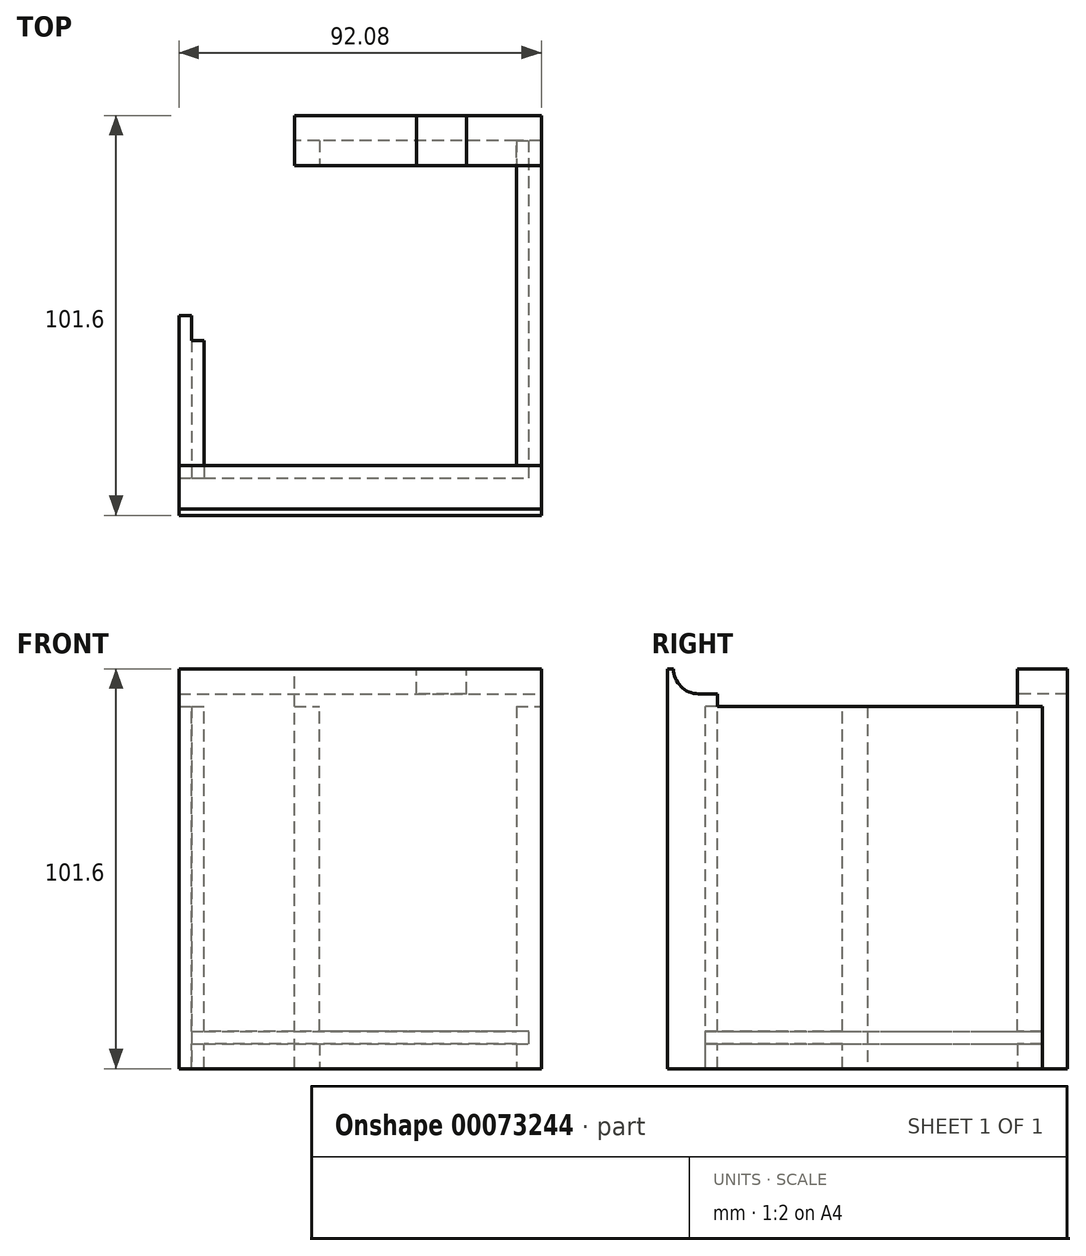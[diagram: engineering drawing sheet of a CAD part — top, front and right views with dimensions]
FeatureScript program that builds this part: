
annotation { "Feature Type Name" : "Feature", "Feature Type Description" : "" }
export const myFeature = defineFeature(function(context is Context, id is Id, definition is map)
    precondition{}
    {
        {
            var Q0;
            Q0=qCreatedBy(makeId("Top.planeOp"),FACE);
            var sketch = newSketch(context, id + "F0", { "sketchPlane" : qUnion([Q0])});
            skLineSegment(sketch, "E0", {"start": v(0, 0) * mm, "end": v(0, -101.6) * mm, "construction": true});
            skLineSegment(sketch, "E1", {"start": v(0, -101.6) * mm, "end": v(-92.08, -101.6) * mm, "construction": true});
            skLineSegment(sketch, "E2", {"start": v(-62.75, 0) * mm, "end": v(0, 0) * mm, "construction": true});
            skLineSegment(sketch, "E3", {"start": v(-92.08, -101.6) * mm, "end": v(-92.08, -50.8) * mm, "construction": true});
            skLineSegment(sketch, "E4", {"start": v(-62.75, 0) * mm, "end": v(-92.08, -50.8) * mm, "construction": true});
            skSolve(sketch);
        }
        {
            var Q0;
            Q0=qCreatedBy(makeId("Front.planeOp"),FACE);
            var sketch = newSketch(context, id + "F1", { "sketchPlane" : qUnion([Q0])});
            skLineSegment(sketch, "E5.bottom", {"start": v(0, 0) * mm, "end": v(-62.75, 0) * mm});
            skLineSegment(sketch, "E5.top", {"start": v(0, 101.6) * mm, "end": v(-62.75, 101.6) * mm});
            skLineSegment(sketch, "E5.left", {"start": v(0, 0) * mm, "end": v(0, 101.6) * mm});
            skLineSegment(sketch, "E5.right", {"start": v(-62.75, 0) * mm, "end": v(-62.75, 101.6) * mm});
            skSolve(sketch);
        }
        {
            var Q0;
            Q0=makeQuery(id+"F1.imprint","IMPRINT",FACE,{"disambiguationData":[TD([[makeQuery(id+"F1.imprint","IMPRINT",EDGE,{"derivedFrom":sQuery(id+"F1.wireOp",EDGE,"E5.bottom")}),-1.0]])]});
            extrude(context, id + "F2", {"entities" : qUnion([Q0]), "depth" : 12.7 * mm});
        }
        {
            var Q0;
            Q0=makeQuery(id+"F2.opExtrude","CAP_FACE",FACE,{"disambiguationData":[OSD([sQuery(id+"F1.wireOp",EDGE,"E5.bottom"),sQuery(id+"F1.wireOp",EDGE,"E5.top"),sQuery(id+"F1.wireOp",EDGE,"E5.left"),sQuery(id+"F1.wireOp",EDGE,"E5.right")])],"isStart":false});
            var sketch = newSketch(context, id + "F3", { "sketchPlane" : qUnion([Q0])});
            skLineSegment(sketch, "E6.bottom", {"start": v(-6.35, 92.08) * mm, "end": v(0, 92.08) * mm});
            skLineSegment(sketch, "E6.top", {"start": v(-6.35, 6.35) * mm, "end": v(0, 6.35) * mm});
            skLineSegment(sketch, "E6.left", {"start": v(-6.35, 92.08) * mm, "end": v(-6.35, 6.35) * mm});
            skLineSegment(sketch, "E6.right", {"start": v(0, 92.08) * mm, "end": v(0, 6.35) * mm});
            skLineSegment(sketch, "E7.bottom", {"start": v(-6.35, 6.35) * mm, "end": v(-62.75, 6.35) * mm});
            skLineSegment(sketch, "E7.top", {"start": v(-6.35, 9.53) * mm, "end": v(-62.75, 9.52) * mm});
            skLineSegment(sketch, "E7.left", {"start": v(-6.35, 6.35) * mm, "end": v(-6.35, 9.53) * mm});
            skLineSegment(sketch, "E7.right", {"start": v(-62.75, 6.35) * mm, "end": v(-62.75, 9.52) * mm});
            skLineSegment(sketch, "E8.bottom", {"start": v(-62.75, 9.52) * mm, "end": v(-56.4, 9.52) * mm});
            skLineSegment(sketch, "E8.top", {"start": v(-62.75, 92.08) * mm, "end": v(-56.4, 92.08) * mm});
            skLineSegment(sketch, "E8.left", {"start": v(-62.75, 9.52) * mm, "end": v(-62.75, 92.08) * mm});
            skLineSegment(sketch, "E8.right", {"start": v(-56.4, 9.52) * mm, "end": v(-56.4, 92.08) * mm});
            skLineSegment(sketch, "E9.bottom", {"start": v(-56.4, 9.52) * mm, "end": v(-62.75, 9.52) * mm});
            skLineSegment(sketch, "E9.top", {"start": v(-56.4, 0) * mm, "end": v(-62.75, 0) * mm});
            skLineSegment(sketch, "E9.left", {"start": v(-56.4, 9.52) * mm, "end": v(-56.4, 0) * mm});
            skLineSegment(sketch, "E9.right", {"start": v(-62.75, 9.52) * mm, "end": v(-62.75, 0) * mm});
            skLineSegment(sketch, "E10.bottom", {"start": v(-6.35, 9.53) * mm, "end": v(0, 9.53) * mm});
            skLineSegment(sketch, "E10.top", {"start": v(-6.35, 0) * mm, "end": v(0, 0) * mm});
            skLineSegment(sketch, "E10.left", {"start": v(-6.35, 9.53) * mm, "end": v(-6.35, 0) * mm});
            skLineSegment(sketch, "E10.right", {"start": v(0, 9.53) * mm, "end": v(0, 0) * mm});
            skSolve(sketch);
        }
        {
            var Q0;
            Q0 = qSketchRegion(id + "F3", true);
            extrude(context, id + "F4", {"entities" : qUnion([Q0]), "operationType" : NewBodyOperationType.REMOVE, "oppositeDirection" : true, "depth" : 6.35 * mm});
        }
        {
            var Q0;
            Q0=makeQuery(id+"F4.boolean.opBoolean","COPY",FACE,{"derivedFrom":makeQuery(id+"F4.opExtrude","CAP_FACE",FACE,{"disambiguationData":[OSD([sQuery(id+"F3.wireOp",EDGE,"E6.bottom"),sQuery(id+"F3.wireOp",EDGE,"E6.left"),sQuery(id+"F3.wireOp",EDGE,"E6.right"),sQuery(id+"F3.wireOp",EDGE,"E7.bottom"),sQuery(id+"F3.wireOp",EDGE,"E7.top"),sQuery(id+"F3.wireOp",EDGE,"E8.top"),sQuery(id+"F3.wireOp",EDGE,"E8.left"),sQuery(id+"F3.wireOp",EDGE,"E8.right"),sQuery(id+"F3.wireOp",EDGE,"E9.top"),sQuery(id+"F3.wireOp",EDGE,"E9.left"),sQuery(id+"F3.wireOp",EDGE,"E9.right"),sQuery(id+"F3.wireOp",EDGE,"E10.top"),sQuery(id+"F3.wireOp",EDGE,"E10.left"),sQuery(id+"F3.wireOp",EDGE,"E10.right")])],"isStart":false})});
            var sketch = newSketch(context, id + "F5", { "sketchPlane" : qUnion([Q0])});
            skLineSegment(sketch, "E11", {"start": v(-6.35, 92.08) * mm, "end": v(0, 92.08) * mm});
            skLineSegment(sketch, "E12", {"start": v(0, 92.08) * mm, "end": v(0, 0) * mm});
            skLineSegment(sketch, "E13", {"start": v(0, 0) * mm, "end": v(-6.35, 0) * mm});
            skLineSegment(sketch, "E14", {"start": v(-6.35, 0) * mm, "end": v(-6.35, 6.35) * mm});
            skLineSegment(sketch, "E15", {"start": v(-6.35, 6.35) * mm, "end": v(-3.17, 6.35) * mm});
            skLineSegment(sketch, "E16", {"start": v(-3.17, 6.35) * mm, "end": v(-3.17, 9.53) * mm});
            skLineSegment(sketch, "E17", {"start": v(-3.17, 9.53) * mm, "end": v(-6.35, 9.53) * mm});
            skLineSegment(sketch, "E18", {"start": v(-6.35, 9.53) * mm, "end": v(-6.35, 92.08) * mm});
            skSolve(sketch);
        }
        {
            var Q0;
            Q0 = qSketchRegion(id + "F5", true);
            extrude(context, id + "F6", {"entities" : qUnion([Q0]), "depth" : 85.72 * mm});
        }
        {
            var Q0;
            Q0=makeQuery(id+"F6.opExtrude","CAP_FACE",FACE,{"disambiguationData":[OSD([sQuery(id+"F5.wireOp",EDGE,"E11"),sQuery(id+"F5.wireOp",EDGE,"E12"),sQuery(id+"F5.wireOp",EDGE,"E13"),sQuery(id+"F5.wireOp",EDGE,"E14"),sQuery(id+"F5.wireOp",EDGE,"E15"),sQuery(id+"F5.wireOp",EDGE,"E16"),sQuery(id+"F5.wireOp",EDGE,"E17"),sQuery(id+"F5.wireOp",EDGE,"E18")])],"isStart":false});
            var sketch = newSketch(context, id + "F7", { "sketchPlane" : qUnion([Q0])});
            skLineSegment(sketch, "E19.bottom", {"start": v(0, 0) * mm, "end": v(-92.08, 0) * mm});
            skLineSegment(sketch, "E19.top", {"start": v(0, 101.6) * mm, "end": v(-92.08, 101.6) * mm});
            skLineSegment(sketch, "E19.left", {"start": v(0, 0) * mm, "end": v(0, 101.6) * mm});
            skLineSegment(sketch, "E19.right", {"start": v(-92.08, 0) * mm, "end": v(-92.08, 101.6) * mm});
            skSolve(sketch);
        }
        {
            var Q0;
            Q0 = qSketchRegion(id + "F7", true);
            extrude(context, id + "F8", {"entities" : qUnion([Q0]), "depth" : 9.52 * mm});
        }
        {
            var Q0;
            Q0=makeQuery(id+"F8.opExtrude","CAP_FACE",FACE,{"disambiguationData":[OSD([sQuery(id+"F7.wireOp",EDGE,"E19.bottom"),sQuery(id+"F7.wireOp",EDGE,"E19.top"),sQuery(id+"F7.wireOp",EDGE,"E19.left"),sQuery(id+"F7.wireOp",EDGE,"E19.right")])],"isStart":true});
            var sketch = newSketch(context, id + "F9", { "sketchPlane" : qUnion([Q0])});
            skLineSegment(sketch, "E20", {"start": v(0, 101.6) * mm, "end": v(92.08, 101.6) * mm});
            skLineSegment(sketch, "E21", {"start": v(92.08, 101.6) * mm, "end": v(92.08, 0) * mm, "construction": true});
            skLineSegment(sketch, "E22", {"start": v(92.08, 0) * mm, "end": v(6.35, 0) * mm});
            skLineSegment(sketch, "E23", {"start": v(6.35, 0) * mm, "end": v(6.35, 6.35) * mm});
            skLineSegment(sketch, "E24", {"start": v(6.35, 6.35) * mm, "end": v(88.9, 6.35) * mm});
            skLineSegment(sketch, "E25", {"start": v(88.9, 6.35) * mm, "end": v(88.9, 9.53) * mm});
            skLineSegment(sketch, "E26", {"start": v(88.9, 9.53) * mm, "end": v(6.35, 9.53) * mm});
            skLineSegment(sketch, "E27", {"start": v(6.35, 9.53) * mm, "end": v(6.35, 92.08) * mm});
            skLineSegment(sketch, "E28", {"start": v(6.35, 92.08) * mm, "end": v(0, 92.08) * mm});
            skLineSegment(sketch, "E29", {"start": v(0, 92.08) * mm, "end": v(0, 101.6) * mm});
            skLineSegment(sketch, "E30", {"start": v(85.73, 0) * mm, "end": v(85.73, 92.08) * mm});
            skLineSegment(sketch, "E31", {"start": v(85.73, 92.08) * mm, "end": v(92.08, 92.08) * mm});
            skLineSegment(sketch, "E32", {"start": v(92.08, 92.08) * mm, "end": v(92.08, 101.6) * mm});
            skSolve(sketch);
        }
        {
            var Q0;
            {var subQ0=sQuery(id+"F9.wireOp",EDGE,"E23");Q0=makeQuery(id+"F9.imprint","IMPRINT",FACE,{"disambiguationData":[TD([[makeQuery(id+"F9.imprint","IMPRINT",EDGE,{"derivedFrom":subQ0}),-1.0]])]});}
            var Q1;
            {var subQ0=sQuery(id+"F9.wireOp",EDGE,"E27");Q1=makeQuery(id+"F9.imprint","IMPRINT",FACE,{"disambiguationData":[TD([[makeQuery(id+"F9.imprint","IMPRINT",EDGE,{"derivedFrom":subQ0}),-1.0]])]});}
            extrude(context, id + "F10", {"entities" : qUnion([Q0, Q1]), "operationType" : NewBodyOperationType.ADD, "depth" : 3.17 * mm});
        }
        {
            var Q0;
            Q0=makeQuery(id+"F10.boolean.opBoolean","MERGE",FACE,{"derivedFrom":[makeQuery(id+"F8.opExtrude","SWEPT_FACE",FACE,{"disambiguationData":[OSD([sQuery(id+"F7.wireOp",EDGE,"E19.left")])]}),makeQuery(id+"F10.opExtrude","SWEPT_FACE",FACE,{"disambiguationData":[OSD([sQuery(id+"F9.wireOp",EDGE,"E29")])]})]});
            var sketch = newSketch(context, id + "F11", { "sketchPlane" : qUnion([Q0])});
            skArc(sketch, "E33", {"start": v(-100.01, 101.6) * mm, "mid": v(-98.15, 97.1) * mm, "end": v(-93.66, 95.25) * mm});
            skLineSegment(sketch, "E34", {"start": v(-100.01, 101.6) * mm, "end": v(-93.66, 101.6) * mm});
            skLineSegment(sketch, "E35", {"start": v(-93.66, 101.6) * mm, "end": v(-88.9, 101.6) * mm});
            skLineSegment(sketch, "E36", {"start": v(-88.9, 101.6) * mm, "end": v(-88.9, 95.25) * mm});
            skLineSegment(sketch, "E37", {"start": v(-88.9, 95.25) * mm, "end": v(-93.66, 95.25) * mm});
            skLineSegment(sketch, "E38", {"start": v(-93.66, 95.25) * mm, "end": v(-93.66, 101.6) * mm, "construction": true});
            skSolve(sketch);
        }
        {
            var Q0;
            Q0 = qSketchRegion(id + "F11", true);
            extrude(context, id + "F12", {"entities" : qUnion([Q0]), "operationType" : NewBodyOperationType.REMOVE, "endBound" : BoundingType.UP_TO_NEXT, "oppositeDirection" : true, "depth" : 25.4 * mm});
        }
        {
            var Q0;
            {var subQ0=sQuery(id+"F1.wireOp",EDGE,"E5.right");var subQ1=sQuery(id+"F1.wireOp",EDGE,"E5.left");var subQ2=sQuery(id+"F1.wireOp",EDGE,"E5.top");Q0=makeQuery(id+"F4.boolean.opBoolean","SPLIT",FACE,{"disambiguationData":[TD([makeQuery(id+"F2.opExtrude","SWEPT_FACE",FACE,{"disambiguationData":[OSD([subQ2])]})])],"derivedFrom":makeQuery(id+"F2.opExtrude","CAP_FACE",FACE,{"disambiguationData":[OSD([sQuery(id+"F1.wireOp",EDGE,"E5.bottom"),subQ2,subQ1,subQ0])],"isStart":false})});}
            var sketch = newSketch(context, id + "F13", { "sketchPlane" : qUnion([Q0])});
            skLineSegment(sketch, "E39.bottom", {"start": v(-31.75, 101.6) * mm, "end": v(-19.05, 101.6) * mm});
            skLineSegment(sketch, "E39.top", {"start": v(-31.75, 95.25) * mm, "end": v(-19.05, 95.25) * mm});
            skLineSegment(sketch, "E39.left", {"start": v(-31.75, 101.6) * mm, "end": v(-31.75, 95.25) * mm});
            skLineSegment(sketch, "E39.right", {"start": v(-19.05, 101.6) * mm, "end": v(-19.05, 95.25) * mm});
            skSolve(sketch);
        }
        {
            var Q0;
            Q0 = qSketchRegion(id + "F13", true);
            extrude(context, id + "F14", {"entities" : qUnion([Q0]), "operationType" : NewBodyOperationType.REMOVE, "endBound" : BoundingType.UP_TO_NEXT, "oppositeDirection" : true, "depth" : 25.4 * mm});
        }
        {
            var Q0;
            Q0=qCreatedBy(makeId("Top.planeOp"),FACE);
            var sketch = newSketch(context, id + "F15", { "sketchPlane" : qUnion([Q0])});
            skLineSegment(sketch, "E40.bottom", {"start": v(-92.08, -50.8) * mm, "end": v(-85.73, -50.8) * mm});
            skLineSegment(sketch, "E40.top", {"start": v(-92.08, -92.08) * mm, "end": v(-85.73, -92.08) * mm});
            skLineSegment(sketch, "E40.left", {"start": v(-92.08, -50.8) * mm, "end": v(-92.08, -92.08) * mm});
            skLineSegment(sketch, "E40.right", {"start": v(-85.73, -50.8) * mm, "end": v(-85.73, -92.08) * mm});
            skSolve(sketch);
        }
        {
            var Q0;
            Q0 = qSketchRegion(id + "F15", true);
            var Q1;
            Q1=makeQuery(id+"F6.opExtrude","SWEPT_FACE",FACE,{"disambiguationData":[OSD([sQuery(id+"F5.wireOp",EDGE,"E11")])]});
            extrude(context, id + "F16", {"entities" : qUnion([Q0]), "endBound" : BoundingType.UP_TO_SURFACE, "endBoundEntityFace" : qUnion([Q1]), "depth" : 25.4 * mm});
        }
        {
            var Q0;
            Q0=makeQuery(id+"F16.opExtrude","SWEPT_FACE",FACE,{"disambiguationData":[OSD([sQuery(id+"F15.wireOp",EDGE,"E40.right")])]});
            var sketch = newSketch(context, id + "F17", { "sketchPlane" : qUnion([Q0])});
            skLineSegment(sketch, "E41.bottom", {"start": v(-50.8, 9.53) * mm, "end": v(-92.08, 9.53) * mm});
            skLineSegment(sketch, "E41.top", {"start": v(-50.8, 6.35) * mm, "end": v(-92.08, 6.35) * mm});
            skLineSegment(sketch, "E41.left", {"start": v(-50.8, 9.52) * mm, "end": v(-50.8, 6.35) * mm});
            skLineSegment(sketch, "E41.right", {"start": v(-92.08, 9.53) * mm, "end": v(-92.08, 6.35) * mm});
            skLineSegment(sketch, "E42.bottom", {"start": v(-50.8, 0) * mm, "end": v(-57.15, 0) * mm});
            skLineSegment(sketch, "E42.top", {"start": v(-50.8, 92.08) * mm, "end": v(-57.15, 92.08) * mm});
            skLineSegment(sketch, "E42.left", {"start": v(-50.8, 0) * mm, "end": v(-50.8, 92.08) * mm});
            skLineSegment(sketch, "E42.right", {"start": v(-57.15, 0) * mm, "end": v(-57.15, 92.08) * mm});
            skSolve(sketch);
        }
        {
            var Q0;
            Q0 = qSketchRegion(id + "F17", true);
            extrude(context, id + "F18", {"entities" : qUnion([Q0]), "operationType" : NewBodyOperationType.REMOVE, "oppositeDirection" : true, "depth" : 3.17 * mm});
        }
    });
